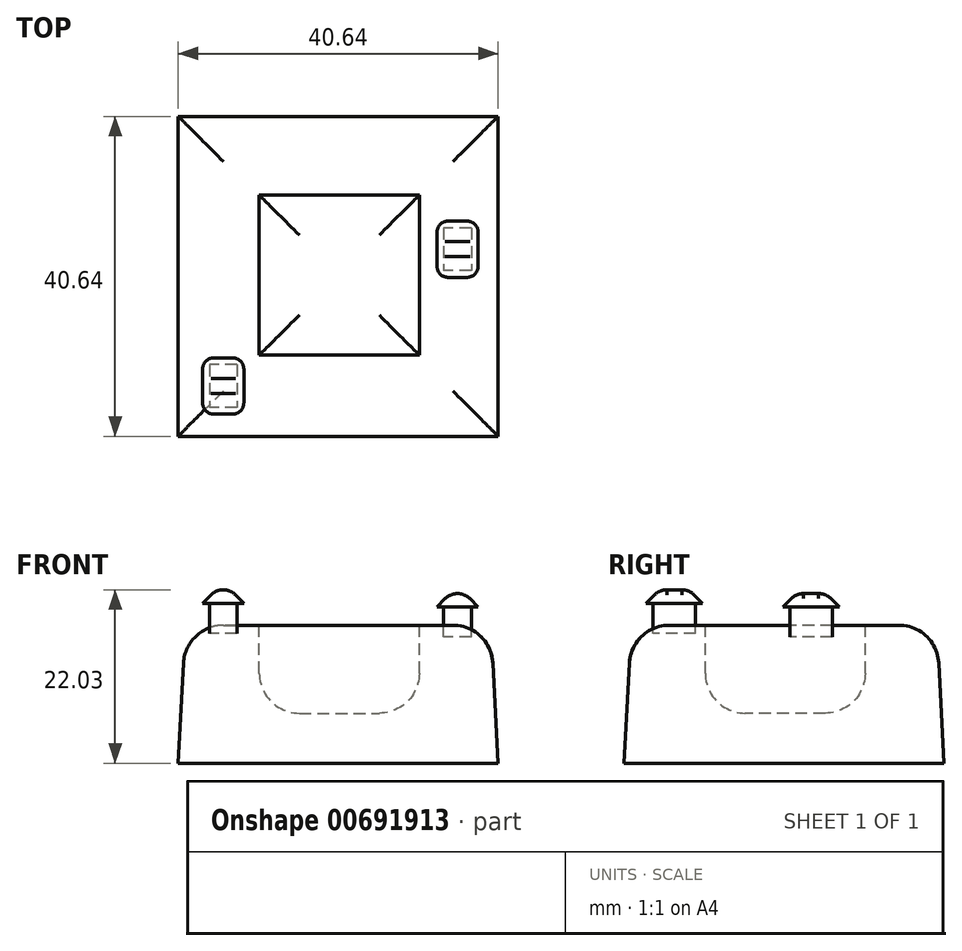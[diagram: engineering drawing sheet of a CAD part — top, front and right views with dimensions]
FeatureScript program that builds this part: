
annotation { "Feature Type Name" : "Feature", "Feature Type Description" : "" }
export const myFeature = defineFeature(function(context is Context, id is Id, definition is map)
    precondition{}
    {
        {
            var Q0;
            Q0=qCreatedBy(makeId("Top.planeOp"),FACE);
            var sketch = newSketch(context, id + "F0", { "sketchPlane" : qUnion([Q0])});
            skLineSegment(sketch, "E0.bottom", {"start": v(-40.64, 35.15) * mm, "end": v(0, 35.15) * mm});
            skLineSegment(sketch, "E0.top", {"start": v(-40.64, -5.49) * mm, "end": v(0, -5.49) * mm});
            skLineSegment(sketch, "E0.left", {"start": v(-40.64, 35.15) * mm, "end": v(-40.64, -5.49) * mm});
            skLineSegment(sketch, "E0.right", {"start": v(0, 35.15) * mm, "end": v(0, -5.49) * mm});
            skSolve(sketch);
        }
        {
            var Q0;
            Q0=makeQuery(id+"F0.imprint","IMPRINT",FACE,{"disambiguationData":[TD([[makeQuery(id+"F0.imprint","IMPRINT",EDGE,{"derivedFrom":sQuery(id+"F0.wireOp",EDGE,"E0.bottom")}),-1.0]])]});
            extrude(context, id + "F1", {"entities" : qUnion([Q0]), "depth" : 17.53 * mm, "offsetDistance" : 25.4 * mm, "hasDraft" : true, "draftAngle" : 3 * degree, "draftPullDirection" : true});
        }
        {
            var Q0;
            Q0=makeQuery(id+"F1.opExtrude","SWEPT_BODY",BODY,{"disambiguationData":[OSD([sQuery(id+"F0.wireOp",EDGE,"E0.bottom"),sQuery(id+"F0.wireOp",EDGE,"E0.top"),sQuery(id+"F0.wireOp",EDGE,"E0.left"),sQuery(id+"F0.wireOp",EDGE,"E0.right")])]});
            transform(context, id + "F2", {"entities" : qUnion([Q0]), "transformType" : TransformType.TRANSLATION_3D, "dx" : 20.32 * mm, "dy" : -14.83 * mm, "dz" : 0 * mm, "makeCopy" : false});
        }
        {
            var Q0;
            Q0=makeQuery(id+"F1.opExtrude","CAP_FACE",FACE,{"disambiguationData":[OSD([sQuery(id+"F0.wireOp",EDGE,"E0.bottom"),sQuery(id+"F0.wireOp",EDGE,"E0.top"),sQuery(id+"F0.wireOp",EDGE,"E0.left"),sQuery(id+"F0.wireOp",EDGE,"E0.right")])],"isStart":false});
            var sketch = newSketch(context, id + "F3", { "sketchPlane" : qUnion([Q0])});
            skLineSegment(sketch, "E1.bottom", {"start": v(-10.02, 10.3) * mm, "end": v(10.3, 10.3) * mm});
            skLineSegment(sketch, "E1.top", {"start": v(-10.02, -10.01) * mm, "end": v(10.3, -10.01) * mm});
            skLineSegment(sketch, "E1.left", {"start": v(-10.02, 10.3) * mm, "end": v(-10.02, -10.01) * mm});
            skLineSegment(sketch, "E1.right", {"start": v(10.3, 10.3) * mm, "end": v(10.3, -10.01) * mm});
            skSolve(sketch);
        }
        {
            var Q0;
            Q0=makeQuery(id+"F3.imprint","IMPRINT",FACE,{"disambiguationData":[TD([[makeQuery(id+"F3.imprint","IMPRINT",EDGE,{"derivedFrom":sQuery(id+"F3.wireOp",EDGE,"E1.bottom")}),-1.0]])]});
            extrude(context, id + "F4", {"entities" : qUnion([Q0]), "operationType" : NewBodyOperationType.REMOVE, "oppositeDirection" : true, "depth" : 11.18 * mm, "offsetDistance" : 25.4 * mm});
        }
        {
            var Q0;
            Q0=makeQuery(id+"F4.boolean.opBoolean","COPY",EDGE,{"derivedFrom":makeQuery(id+"F4.opExtrude","CAP_EDGE",EDGE,{"disambiguationData":[OSD([sQuery(id+"F3.wireOp",EDGE,"E1.bottom")])],"isStart":true})});
            var Q1;
            Q1=makeQuery(id+"F4.boolean.opBoolean","COPY",EDGE,{"derivedFrom":makeQuery(id+"F4.opExtrude","CAP_EDGE",EDGE,{"disambiguationData":[OSD([sQuery(id+"F3.wireOp",EDGE,"E1.left")])],"isStart":true})});
            var Q2;
            Q2=makeQuery(id+"F4.boolean.opBoolean","COPY",EDGE,{"derivedFrom":makeQuery(id+"F4.opExtrude","CAP_EDGE",EDGE,{"disambiguationData":[OSD([sQuery(id+"F3.wireOp",EDGE,"E1.top")])],"isStart":true})});
            var Q3;
            Q3=makeQuery(id+"F4.boolean.opBoolean","COPY",EDGE,{"derivedFrom":makeQuery(id+"F4.opExtrude","CAP_EDGE",EDGE,{"disambiguationData":[OSD([sQuery(id+"F3.wireOp",EDGE,"E1.right")])],"isStart":true})});
            var Q4;
            Q4=makeQuery(id+"F4.boolean.opBoolean","COPY",EDGE,{"derivedFrom":makeQuery(id+"F4.opExtrude","CAP_EDGE",EDGE,{"disambiguationData":[OSD([sQuery(id+"F3.wireOp",EDGE,"E1.bottom")])],"isStart":false})});
            var Q5;
            Q5=makeQuery(id+"F4.boolean.opBoolean","COPY",EDGE,{"derivedFrom":makeQuery(id+"F4.opExtrude","CAP_EDGE",EDGE,{"disambiguationData":[OSD([sQuery(id+"F3.wireOp",EDGE,"E1.left")])],"isStart":false})});
            var Q6;
            Q6=makeQuery(id+"F4.boolean.opBoolean","COPY",EDGE,{"derivedFrom":makeQuery(id+"F4.opExtrude","CAP_EDGE",EDGE,{"disambiguationData":[OSD([sQuery(id+"F3.wireOp",EDGE,"E1.right")])],"isStart":false})});
            var Q7;
            Q7=makeQuery(id+"F4.boolean.opBoolean","COPY",EDGE,{"derivedFrom":makeQuery(id+"F4.opExtrude","CAP_EDGE",EDGE,{"disambiguationData":[OSD([sQuery(id+"F3.wireOp",EDGE,"E1.top")])],"isStart":false})});
            fillet(context, id + "F5", {"entities" : qUnion([Q0, Q1, Q2, Q3, Q4, Q5, Q6, Q7]), "radius" : 5.08 * mm, "tangentPropagation" : true, "allowEdgeOverflow" : false});
        }
        {
            var Q0;
            Q0=makeQuery(id+"F1.opExtrude","CAP_EDGE",EDGE,{"disambiguationData":[OSD([sQuery(id+"F0.wireOp",EDGE,"E0.right")])],"isStart":false});
            var Q1;
            Q1=makeQuery(id+"F1.opExtrude","CAP_EDGE",EDGE,{"disambiguationData":[OSD([sQuery(id+"F0.wireOp",EDGE,"E0.top")])],"isStart":false});
            var Q2;
            Q2=makeQuery(id+"F1.opExtrude","CAP_EDGE",EDGE,{"disambiguationData":[OSD([sQuery(id+"F0.wireOp",EDGE,"E0.left")])],"isStart":false});
            var Q3;
            Q3=makeQuery(id+"F1.opExtrude","CAP_EDGE",EDGE,{"disambiguationData":[OSD([sQuery(id+"F0.wireOp",EDGE,"E0.bottom")])],"isStart":false});
            fillet(context, id + "F6", {"entities" : qUnion([Q0, Q1, Q2, Q3]), "radius" : 5.08 * mm, "tangentPropagation" : true, "allowEdgeOverflow" : false});
        }
        {
            var Q0;
            Q0=qCreatedBy(makeId("Top.planeOp"),FACE);
            var sketch = newSketch(context, id + "F7", { "sketchPlane" : qUnion([Q0])});
            skLineSegment(sketch, "E2.bottom", {"start": v(41.7, 5.91) * mm, "end": v(44.04, 5.91) * mm});
            skLineSegment(sketch, "E2.top", {"start": v(41.7, 2.3) * mm, "end": v(44.04, 2.3) * mm});
            skLineSegment(sketch, "E2.left", {"start": v(41.7, 5.91) * mm, "end": v(41.7, 2.3) * mm});
            skLineSegment(sketch, "E2.right", {"start": v(44.04, 5.91) * mm, "end": v(44.04, 2.3) * mm});
            skSolve(sketch);
        }
        {
            var Q0;
            Q0=makeQuery(id+"F7.imprint","IMPRINT",FACE,{"disambiguationData":[TD([[makeQuery(id+"F7.imprint","IMPRINT",EDGE,{"derivedFrom":sQuery(id+"F7.wireOp",EDGE,"E2.bottom")}),-1.0]])]});
            extrude(context, id + "F8", {"entities" : qUnion([Q0]), "depth" : 2.54 * mm, "offsetDistance" : 25.4 * mm});
        }
        {
            var Q0;
            Q0=qCreatedBy(makeId("Top.planeOp"),FACE);
            var sketch = newSketch(context, id + "F9", { "sketchPlane" : qUnion([Q0])});
            skLineSegment(sketch, "E3.0", {"start": v(41.12, 1.72) * mm, "end": v(41.12, 6.5) * mm});
            skLineSegment(sketch, "E3.1", {"start": v(44.63, 1.72) * mm, "end": v(41.12, 1.72) * mm});
            skLineSegment(sketch, "E3.2", {"start": v(44.63, 6.5) * mm, "end": v(44.63, 1.72) * mm});
            skLineSegment(sketch, "E3.3", {"start": v(41.12, 6.5) * mm, "end": v(44.63, 6.5) * mm});
            skSolve(sketch);
        }
        {
            var Q0;
            Q0=makeQuery(id+"F9.imprint","IMPRINT",FACE,{"disambiguationData":[TD([[makeQuery(id+"F9.imprint","IMPRINT",EDGE,{"derivedFrom":sQuery(id+"F9.wireOp",EDGE,"E3.0")}),-1.0]])]});
            extrude(context, id + "F10", {"entities" : qUnion([Q0]), "operationType" : NewBodyOperationType.ADD, "oppositeDirection" : true, "depth" : 3.96 * mm, "offsetDistance" : 25.4 * mm, "hasDraft" : true, "draftAngle" : 45 * degree, "draftPullDirection" : true});
        }
        {
            var Q0;
            Q0=makeQuery(id+"F10.opExtrude","SWEPT_EDGE",EDGE,{"disambiguationData":[OSD([sQuery(id+"F9.wireOp",EDGE,"E3.1"),sQuery(id+"F9.wireOp",EDGE,"E3.2")])]});
            var Q1;
            Q1=makeQuery(id+"F10.opExtrude","SWEPT_EDGE",EDGE,{"disambiguationData":[OSD([sQuery(id+"F9.wireOp",EDGE,"E3.0"),sQuery(id+"F9.wireOp",EDGE,"E3.1")])]});
            var Q2;
            Q2=makeQuery(id+"F10.*.draft.opDraft","TWEAK_EDGE",EDGE,{"derivedFrom":[makeQuery(id+"F10.opExtrude","SWEPT_FACE",FACE,{"disambiguationData":[OSD([sQuery(id+"F9.wireOp",EDGE,"E3.0")])]}),makeQuery(id+"F10.opExtrude","SWEPT_FACE",FACE,{"disambiguationData":[OSD([sQuery(id+"F9.wireOp",EDGE,"E3.2")])]})]});
            var Q3;
            Q3=makeQuery(id+"F10.opExtrude","SWEPT_EDGE",EDGE,{"disambiguationData":[OSD([sQuery(id+"F9.wireOp",EDGE,"E3.0"),sQuery(id+"F9.wireOp",EDGE,"E3.3")])]});
            var Q4;
            Q4=makeQuery(id+"F10.opExtrude","SWEPT_EDGE",EDGE,{"disambiguationData":[OSD([sQuery(id+"F9.wireOp",EDGE,"E3.2"),sQuery(id+"F9.wireOp",EDGE,"E3.3")])]});
            fillet(context, id + "F11", {"entities" : qUnion([Q0, Q1, Q2, Q3, Q4]), "radius" : 1.48 * mm, "tangentPropagation" : true, "allowEdgeOverflow" : false});
        }
        {
            var Q0;
            Q0=makeQuery(id+"F8.opExtrude","SWEPT_BODY",BODY,{"disambiguationData":[OSD([sQuery(id+"F7.wireOp",EDGE,"E2.bottom"),sQuery(id+"F7.wireOp",EDGE,"E2.top"),sQuery(id+"F7.wireOp",EDGE,"E2.left"),sQuery(id+"F7.wireOp",EDGE,"E2.right")])]});
            transform(context, id + "F12", {"entities" : qUnion([Q0]), "transformType" : TransformType.TRANSLATION_3D, "dx" : -19.05 * mm, "dy" : 0 * mm, "dz" : 40.4 * mm, "makeCopy" : false});
        }
        {
            var Q0;
            Q0=makeQuery(id+"F8.opExtrude","SWEPT_BODY",BODY,{"disambiguationData":[OSD([sQuery(id+"F7.wireOp",EDGE,"E2.bottom"),sQuery(id+"F7.wireOp",EDGE,"E2.top"),sQuery(id+"F7.wireOp",EDGE,"E2.left"),sQuery(id+"F7.wireOp",EDGE,"E2.right")])]});
            var Q1;
            {var subQ0=sQuery(id+"F0.wireOp",EDGE,"E0.right");Q1=makeQuery(id+"F6.opFillet","BLEND_EDGE",EDGE,{"blendedFrom":[makeQuery(id+"F1.opExtrude","CAP_EDGE",EDGE,{"disambiguationData":[OSD([subQ0])],"isStart":false}),makeQuery(id+"F1.opExtrude","SWEPT_FACE",FACE,{"disambiguationData":[OSD([subQ0])]})],"blendedInto":[makeQuery(id+"F1.opExtrude","SWEPT_FACE",FACE,{"disambiguationData":[OSD([subQ0])]})]});}
            transform(context, id + "F13", {"entities" : qUnion([Q0]), "transformType" : TransformType.ROTATION, "transformAxis" : qUnion([Q1]), "angle" : 180 * degree, "oppositeDirection" : true, "makeCopy" : false});
        }
        {
            var Q0;
            Q0=makeQuery(id+"F8.opExtrude","SWEPT_BODY",BODY,{"disambiguationData":[OSD([sQuery(id+"F7.wireOp",EDGE,"E2.bottom"),sQuery(id+"F7.wireOp",EDGE,"E2.top"),sQuery(id+"F7.wireOp",EDGE,"E2.left"),sQuery(id+"F7.wireOp",EDGE,"E2.right")])]});
            transform(context, id + "F14", {"entities" : qUnion([Q0]), "transformType" : TransformType.TRANSLATION_3D, "dx" : -0.79 * mm, "dy" : 0 * mm, "dz" : 34.34 * mm, "makeCopy" : false});
        }
        {
            var Q0;
            Q0=makeQuery(id+"F8.opExtrude","SWEPT_BODY",BODY,{"disambiguationData":[OSD([sQuery(id+"F7.wireOp",EDGE,"E2.bottom"),sQuery(id+"F7.wireOp",EDGE,"E2.top"),sQuery(id+"F7.wireOp",EDGE,"E2.left"),sQuery(id+"F7.wireOp",EDGE,"E2.right")])]});
            var Q1;
            {var subQ0=sQuery(id+"F9.wireOp",EDGE,"E3.3");var subQ1=sQuery(id+"F9.wireOp",EDGE,"E3.2");Q1=makeQuery(id+"F11.opFillet","BLEND_VERTEX",VERTEX,{"blendedFrom":[makeQuery(id+"F10.opExtrude","SWEPT_EDGE",EDGE,{"disambiguationData":[OSD([subQ1,subQ0])]}),makeQuery(id+"F10.opExtrude","SWEPT_FACE",FACE,{"disambiguationData":[OSD([subQ1])]}),makeQuery(id+"F10.opExtrude","CAP_FACE",FACE,{"disambiguationData":[OSD([sQuery(id+"F9.wireOp",EDGE,"E3.0"),sQuery(id+"F9.wireOp",EDGE,"E3.1"),subQ1,subQ0])],"isStart":true})],"blendedInto":[makeQuery(id+"F10.opExtrude","SWEPT_FACE",FACE,{"disambiguationData":[OSD([subQ1])]}),makeQuery(id+"F10.opExtrude","CAP_FACE",FACE,{"disambiguationData":[OSD([sQuery(id+"F9.wireOp",EDGE,"E3.0"),sQuery(id+"F9.wireOp",EDGE,"E3.1"),subQ1,subQ0])],"isStart":true})]});}
            transform(context, id + "F15", {"entities" : qUnion([Q0]), "transformType" : TransformType.SCALE_UNIFORMLY, "scale" : 1.5, "scalePoint" : qUnion([Q1]), "makeCopy" : false});
        }
        {
            var Q0;
            Q0=makeQuery(id+"F8.opExtrude","SWEPT_BODY",BODY,{"disambiguationData":[OSD([sQuery(id+"F7.wireOp",EDGE,"E2.bottom"),sQuery(id+"F7.wireOp",EDGE,"E2.top"),sQuery(id+"F7.wireOp",EDGE,"E2.left"),sQuery(id+"F7.wireOp",EDGE,"E2.right")])]});
            transform(context, id + "F16", {"entities" : qUnion([Q0]), "transformType" : TransformType.TRANSLATION_3D, "dx" : -0.4 * mm, "dy" : 0 * mm, "dz" : 1.24 * mm, "makeCopy" : false});
        }
        {
            var Q0;
            Q0=makeQuery(id+"F8.opExtrude","SWEPT_BODY",BODY,{"disambiguationData":[OSD([sQuery(id+"F7.wireOp",EDGE,"E2.bottom"),sQuery(id+"F7.wireOp",EDGE,"E2.top"),sQuery(id+"F7.wireOp",EDGE,"E2.left"),sQuery(id+"F7.wireOp",EDGE,"E2.right")])]});
            transform(context, id + "F17", {"entities" : qUnion([Q0]), "transformType" : TransformType.TRANSLATION_3D, "dx" : 0 * mm, "dy" : 0 * mm, "dz" : -0.79 * mm, "makeCopy" : false});
        }
        {
            var Q0;
            Q0=makeQuery(id+"F8.opExtrude","SWEPT_BODY",BODY,{"disambiguationData":[OSD([sQuery(id+"F7.wireOp",EDGE,"E2.bottom"),sQuery(id+"F7.wireOp",EDGE,"E2.top"),sQuery(id+"F7.wireOp",EDGE,"E2.left"),sQuery(id+"F7.wireOp",EDGE,"E2.right")])]});
            transform(context, id + "F18", {"entities" : qUnion([Q0]), "transformType" : TransformType.TRANSLATION_3D, "dx" : -29.77 * mm, "dy" : -17.37 * mm, "dz" : 0.48 * mm, "makeCopy" : true});
        }
    });
